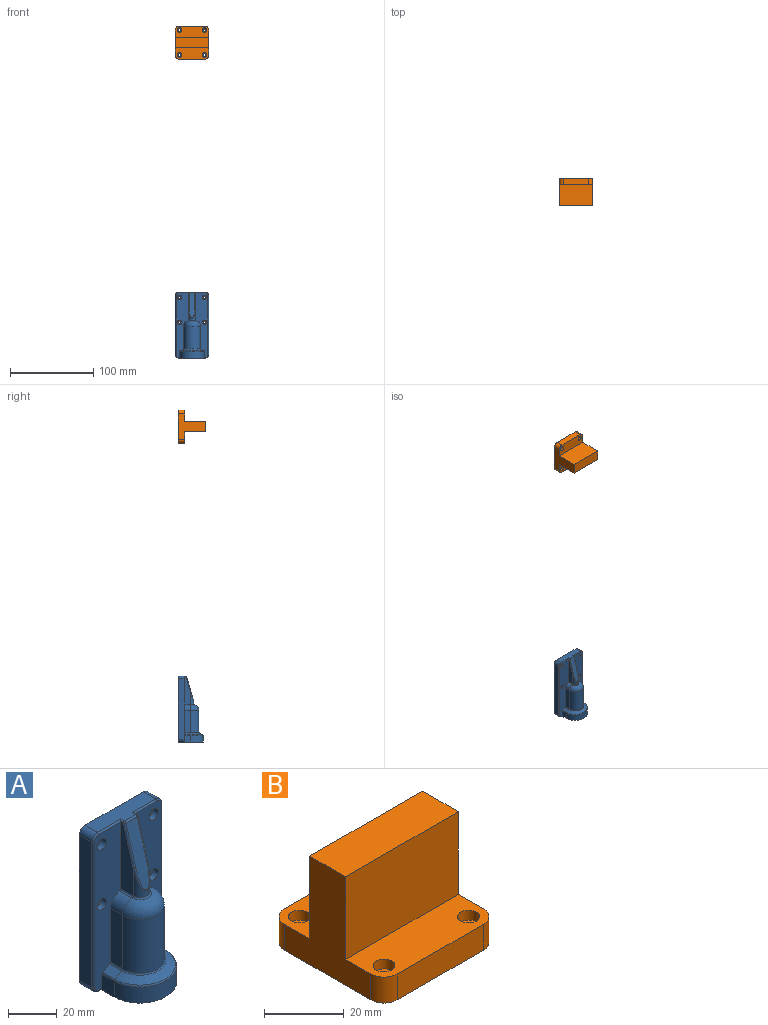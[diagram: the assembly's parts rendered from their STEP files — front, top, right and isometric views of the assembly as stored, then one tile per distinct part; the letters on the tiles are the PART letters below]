
ASSEMBLY  parts=2 mates=1
PART A: 77 faces, bbox 40.5x31.2x79.9 mm
  f0: plane 25x25mm, normal (0,0,-1), area 383.9mm2, adj f67,f68,f69,f70,f71,f72,f73
  f1: cylinder r=1.5mm len=5mm, axis (0,1,0), area 47.1mm2, adj f11,f34
  f2: cylinder r=1.5mm len=5mm, axis (0,1,0), area 47.1mm2, adj f11,f28
  f3: cylinder r=1.5mm len=5mm, axis (0,1,0), area 47.1mm2, adj f11,f30
  f4: cylinder r=1.5mm len=5mm, axis (0,1,0), area 47.1mm2, adj f11,f32
  f5: plane 30.75x8.8mm, normal (0,-0.96,0.28), area 189.1mm2, adj f45,f47,f49,f50
  f6: plane 33.38x7mm, normal (-1,0,0), area 179mm2, adj f13,f21,f45,f46,f64
  f7: plane 27x7mm, normal (-1,0,0), area 189mm2, adj f13,f20,f24,f58
  f8: plane 27x7mm, normal (1,0,0), area 189mm2, adj f15,f20,f22,f60
  f9: plane 7.97x7.79mm, normal (1,0,0), area 55.9mm2, adj f15,f17,f19,f57,f63
  f10: plane 33.65x9.4mm, normal (0,0,1), area 256.6mm2, adj f11,f38,f39,f44,f46,f50,f52,f53
  f11: plane 79.38x40mm, normal (0,1,0), area 3138.1mm2, adj f1,f2,f3,f4,f10,f12,f16,f17
  f12: plane 73.03x7.21mm, normal (-1,0,0), area 526.2mm2, adj f11,f36,f38,f42
  f13: plane 77.79x15.21mm, normal (0,-1,0), area 834mm2, adj f6,f7,f14,f24,f27,f33,f35,f40
  f14: plane 7.97x7.79mm, normal (-1,0,0), area 55.9mm2, adj f13,f17,f19,f40,f61
  f15: plane 77.79x15.21mm, normal (0,-1,0), area 834mm2, adj f8,f9,f18,f22,f25,f29,f31,f53
  f16: plane 73.03x7.21mm, normal (1,0,0), area 526.2mm2, adj f11,f37,f39,f55
  f17: plane 33.65x30mm, normal (0,0,-1), area 338.9mm2, adj f9,f11,f14,f19,f36,f37,f40,f57
  f18: plane 33.38x7mm, normal (1,0,0), area 179mm2, adj f15,f21,f49,f52,f65
  f19: cylinder r=15mm len=30mm, axis (0,0,-1), area 375.6mm2, adj f9,f14,f17,f62
  f20: cylinder r=10mm len=27mm, axis (0,0,-1), area 848.2mm2, adj f7,f8,f23,f59
  f21: cylinder r=4mm len=13.83mm, axis (0,0,1), area 84.2mm2, adj f6,f18,f47,f66
  f22: cylinder r=6mm len=7mm, axis (0,1,0), area 61.1mm2, adj f8,f15,f23,f65
  f23: torus R=4mm, axis (0,0,-1), area 221.9mm2, adj f20,f22,f24,f66
  f24: cylinder r=6mm len=7mm, axis (0,-1,0), area 61.1mm2, adj f7,f13,f23,f64
  f25: plane 7x4.12mm, normal (0.45,0,0.89), area 32.3mm2, adj f15,f26,f60,f63
  f26: cone r=9.92mm half-angle=63.4deg, axis (0,0,-1), area 181mm2, adj f25,f27,f59,f62
  f27: plane 7x4.12mm, normal (-0.45,0,0.89), area 32.3mm2, adj f13,f26,f58,f61
  f28: plane 5.5x5.5mm, normal (0,-1,0), area 16.7mm2, adj f2,f29
  f29: cylinder r=2.75mm len=5.5mm, axis (0,-1,0), area 51.8mm2, adj f15,f28
  f30: plane 5.5x5.5mm, normal (0,-1,0), area 16.7mm2, adj f3,f31
  f31: cylinder r=2.75mm len=5.5mm, axis (0,-1,0), area 51.8mm2, adj f15,f30
  f32: plane 5.5x5.5mm, normal (0,-1,0), area 16.7mm2, adj f4,f33
  f33: cylinder r=2.75mm len=5.5mm, axis (0,-1,0), area 51.8mm2, adj f13,f32
  f34: plane 5.5x5.5mm, normal (0,-1,0), area 16.7mm2, adj f1,f35
  f35: cylinder r=2.75mm len=5.5mm, axis (0,-1,0), area 51.8mm2, adj f13,f34
  f36: cylinder r=3.17mm len=7.21mm, axis (0,-1,0), area 35.9mm2, adj f11,f12,f17,f41
  f37: cylinder r=3.17mm len=7.21mm, axis (0,1,0), area 35.9mm2, adj f11,f16,f17,f56
  f38: cylinder r=3.17mm len=7.21mm, axis (0,1,0), area 35.9mm2, adj f10,f11,f12,f43
  f39: cylinder r=3.17mm len=7.21mm, axis (0,-1,0), area 35.9mm2, adj f10,f11,f16,f54
  f40: cylinder r=0.79mm len=1.83mm, axis (1,0,0), area 2.3mm2, adj f13,f14,f17,f41
  f41: torus R=2.38mm, axis (0,-1,0), area 5.7mm2, adj f13,f36,f40,f42
  f42: cylinder r=0.79mm len=73.03mm, axis (0,0,-1), area 91mm2, adj f12,f13,f41,f43
  f43: torus R=2.38mm, axis (0,-1,0), area 5.7mm2, adj f13,f38,f42,f44
  f44: cylinder r=0.79mm len=13.62mm, axis (-1,0,0), area 16.4mm2, adj f10,f13,f43,f46
  f45: cylinder r=0.79mm len=19.77mm, axis (0,-0.28,-0.96), area 25.4mm2, adj f5,f6,f47,f48
  f46: cylinder r=0.79mm len=2.2mm, axis (0,-1,0), area 2.1mm2, adj f6,f10,f44,f48
  f47: bspline ~13.4x8.18mm, area 20.1mm2, adj f5,f21,f45,f49
  f48: sphere r=0.79mm, area 0.8mm2, adj f45,f46,f50
  f49: cylinder r=0.79mm len=19.77mm, axis (0,0.28,0.96), area 25.4mm2, adj f5,f18,f47,f51
  f50: cylinder r=0.79mm len=6.41mm, axis (1,0,0), area 6.6mm2, adj f5,f10,f48,f51
  f51: sphere r=0.79mm, area 0.8mm2, adj f49,f50,f52
  f52: cylinder r=0.79mm len=2.2mm, axis (0,-1,0), area 2.1mm2, adj f10,f18,f51,f53
  f53: cylinder r=0.79mm len=13.62mm, axis (-1,0,0), area 16.4mm2, adj f10,f15,f52,f54
  f54: torus R=2.38mm, axis (0,-1,0), area 5.7mm2, adj f15,f39,f53,f55
  f55: cylinder r=0.79mm len=73.03mm, axis (0,0,-1), area 91mm2, adj f15,f16,f54,f56
  f56: torus R=2.38mm, axis (0,-1,0), area 5.7mm2, adj f15,f37,f55,f57
  f57: cylinder r=0.79mm len=1.83mm, axis (1,0,0), area 2.3mm2, adj f9,f15,f17,f56
  f58: cylinder r=0.79mm len=7mm, axis (0,-1,0), area 6.2mm2, adj f7,f13,f27,f59
  f59: torus R=10.79mm, axis (0,0,1), area 28mm2, adj f20,f26,f58,f60
  f60: cylinder r=0.79mm len=7mm, axis (0,-1,0), area 6.2mm2, adj f8,f15,f25,f59
  f61: cylinder r=0.79mm len=7mm, axis (0,1,0), area 6.2mm2, adj f13,f14,f27,f62
  f62: torus R=14.21mm, axis (0,0,1), area 41mm2, adj f19,f26,f61,f63
  f63: cylinder r=0.79mm len=7mm, axis (0,-1,0), area 6.2mm2, adj f9,f15,f25,f62
  f64: cylinder r=0.79mm len=7mm, axis (0,-1,0), area 8.1mm2, adj f6,f13,f24,f66
  f65: cylinder r=0.79mm len=7mm, axis (0,1,0), area 8.1mm2, adj f15,f18,f22,f66
  f66: torus R=4.79mm, axis (0,0,1), area 15.4mm2, adj f21,f23,f64,f65
  f67: cylinder r=12.5mm len=25mm, axis (0,0,-1), area 392.7mm2, adj f0,f17
  f68: plane 5.56x5.5mm, normal (-0.87,0.5,0), area 35.3mm2, adj f0,f69,f73,f74
  f69: plane 6.42x5.5mm, normal (0,1,0), area 35.3mm2, adj f0,f68,f70,f74
  f70: plane 5.56x5.5mm, normal (0.87,0.5,0), area 35.3mm2, adj f0,f69,f71,f74
  f71: plane 5.56x5.5mm, normal (0.87,-0.5,0), area 35.3mm2, adj f0,f70,f72,f74
  f72: plane 6.42x5.5mm, normal (0,-1,0), area 35.3mm2, adj f0,f71,f73,f74
  f73: plane 5.56x5.5mm, normal (-0.87,-0.5,0), area 35.3mm2, adj f0,f68,f72,f74
  f74: plane 12.83x11.11mm, normal (0,0,-1), area 66.9mm2, adj f68,f69,f70,f71,f72,f73,f75
  f75: cylinder r=3.57mm len=31.75mm, axis (0,0,-1), area 711.9mm2, adj f74,f76
  f76: plane 7.14x7.14mm, normal (0,0,-1), area 40mm2, adj f75
PART B: 26 faces, bbox 40x40x33.3 mm
  f0: cylinder r=1.5mm len=4.94mm, axis (0,0,-1), area 46.5mm2, adj f5,f20
  f1: cylinder r=1.5mm len=4.94mm, axis (0,0,-1), area 46.5mm2, adj f5,f18
  f2: cylinder r=1.5mm len=4.94mm, axis (0,0,-1), area 46.5mm2, adj f5,f16
  f3: cylinder r=1.5mm len=4.94mm, axis (0,0,-1), area 46.5mm2, adj f5,f14
  f4: plane 30.45x7.94mm, normal (0,-1,0), area 241.7mm2, adj f5,f11,f23,f25
  f5: plane 40x40mm, normal (0,0,-1), area 1552.2mm2, adj f0,f1,f2,f3,f4,f6,f12,f13
  f6: plane 30.45x7.94mm, normal (0,1,0), area 241.7mm2, adj f5,f7,f22,f24
  f7: plane 40x13.65mm, normal (0,0,1), area 488.7mm2, adj f6,f8,f12,f13,f15,f17,f22,f24
  f8: plane 40x25.4mm, normal (0,1,0), area 1016mm2, adj f7,f9,f12,f13
  f9: plane 40x12.7mm, normal (0,0,1), area 508mm2, adj f8,f10,f12,f13
  f10: plane 40x25.4mm, normal (0,-1,0), area 1016mm2, adj f9,f11,f12,f13
  f11: plane 40x13.65mm, normal (0,0,1), area 488.7mm2, adj f4,f10,f12,f13,f19,f21,f23,f25
  f12: plane 33.34x30.45mm, normal (1,0,0), area 564.3mm2, adj f5,f7,f8,f9,f10,f11,f24,f25
  f13: plane 33.34x30.45mm, normal (-1,0,0), area 564.3mm2, adj f5,f7,f8,f9,f10,f11,f22,f23
  f14: plane 5.5x5.5mm, normal (0,0,1), area 16.7mm2, adj f3,f15
  f15: cylinder r=2.75mm len=5.5mm, axis (0,0,1), area 51.8mm2, adj f7,f14
  f16: plane 5.5x5.5mm, normal (0,0,1), area 16.7mm2, adj f2,f17
  f17: cylinder r=2.75mm len=5.5mm, axis (0,0,1), area 51.8mm2, adj f7,f16
  f18: plane 5.5x5.5mm, normal (0,0,1), area 16.7mm2, adj f1,f19
  f19: cylinder r=2.75mm len=5.5mm, axis (0,0,1), area 51.8mm2, adj f11,f18
  f20: plane 5.5x5.5mm, normal (0,0,1), area 16.7mm2, adj f0,f21
  f21: cylinder r=2.75mm len=5.5mm, axis (0,0,1), area 51.8mm2, adj f11,f20
  f22: cylinder r=4.78mm len=7.94mm, axis (0,0,1), area 59.5mm2, adj f5,f6,f7,f13
  f23: cylinder r=4.78mm len=7.94mm, axis (0,0,-1), area 59.5mm2, adj f4,f5,f11,f13
  f24: cylinder r=4.78mm len=7.94mm, axis (0,0,-1), area 59.5mm2, adj f5,f6,f7,f12
  f25: cylinder r=4.78mm len=7.94mm, axis (0,0,1), area 59.5mm2, adj f4,f5,f11,f12
PLACE A t=(0,-3.17,0)mm
PLACE B rot(axis=(1,0,0),90deg) t=(0,-0.06,380)mm
MATE fastened B.f1 <-> A.f15  axis (0,-1,0) through (15,-8,365)mm
